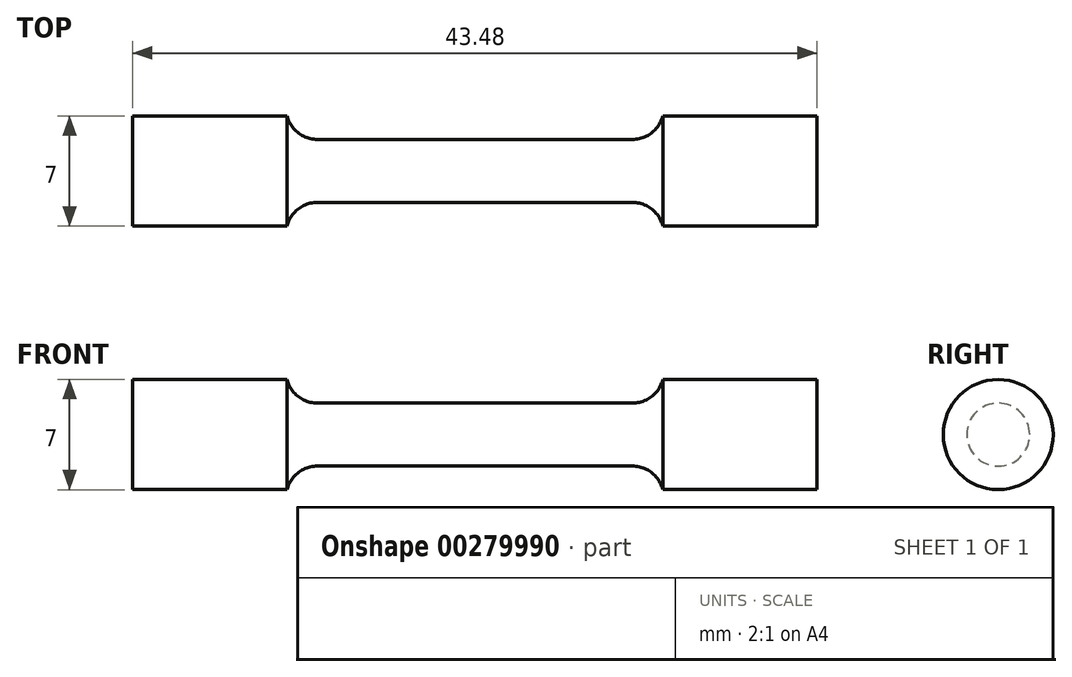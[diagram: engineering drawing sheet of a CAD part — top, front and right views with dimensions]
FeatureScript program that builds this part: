
annotation { "Feature Type Name" : "Feature", "Feature Type Description" : "" }
export const myFeature = defineFeature(function(context is Context, id is Id, definition is map)
    precondition{}
    {
        {
            var Q0;
            Q0=qCreatedBy(makeId("Front.planeOp"),FACE);
            var sketch = newSketch(context, id + "F0", { "sketchPlane" : qUnion([Q0])});
            skLineSegment(sketch, "E0", {"start": v(0, 2) * mm, "end": v(10, 2) * mm});
            skArc(sketch, "E1", {"start": v(10, 2) * mm, "mid": v(11.22, 2.42) * mm, "end": v(11.94, 3.5) * mm});
            skLineSegment(sketch, "E2", {"start": v(11.94, 3.5) * mm, "end": v(21.74, 3.5) * mm});
            skLineSegment(sketch, "E3", {"start": v(21.74, 3.5) * mm, "end": v(21.74, 0) * mm});
            skLineSegment(sketch, "E4.MirrorCS", {"start": v(0, 2) * mm, "end": v(-10, 2) * mm});
            skLineSegment(sketch, "E5.MirrorCS", {"start": v(-21.74, 3.5) * mm, "end": v(-21.74, 0) * mm});
            skLineSegment(sketch, "E6.MirrorCS", {"start": v(-11.94, 3.5) * mm, "end": v(-21.74, 3.5) * mm});
            skArc(sketch, "E7.MirrorCS", {"start": v(-10, 2) * mm, "mid": v(-11.22, 2.42) * mm, "end": v(-11.94, 3.5) * mm});
            skLineSegment(sketch, "E8", {"start": v(-21.74, 0) * mm, "end": v(21.74, 0) * mm});
            skSolve(sketch);
        }
        {
            var Q0;
            Q0 = qSketchRegion(id + "F0", true);
            var Q1;
            Q1=sQuery(id+"F0.wireOp",EDGE,"E8");
            revolve(context, id + "F1", {"entities" : qUnion([Q0]), "axis" : qUnion([Q1]), "revolveType" : RevolveType.FULL});
        }
    });
